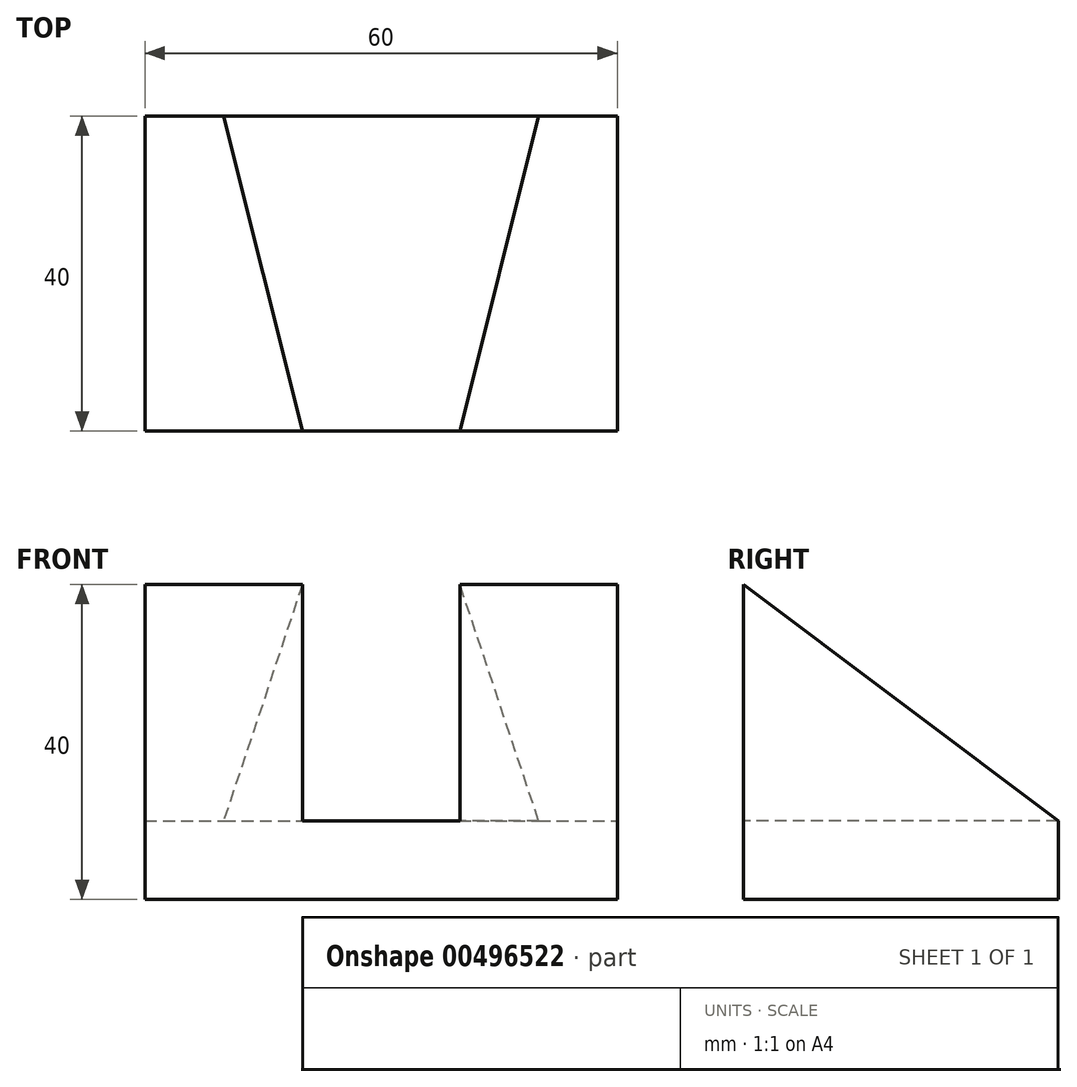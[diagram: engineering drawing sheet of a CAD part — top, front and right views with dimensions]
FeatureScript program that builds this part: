
annotation { "Feature Type Name" : "Feature", "Feature Type Description" : "" }
export const myFeature = defineFeature(function(context is Context, id is Id, definition is map)
    precondition{}
    {
        {
            var Q0;
            Q0=qCreatedBy(makeId("Top.planeOp"),FACE);
            var sketch = newSketch(context, id + "F0", { "sketchPlane" : qUnion([Q0])});
            skLineSegment(sketch, "E0", {"start": v(0, 0) * mm, "end": v(0, 40) * mm});
            skLineSegment(sketch, "E1", {"start": v(0, 40) * mm, "end": v(60, 40) * mm});
            skLineSegment(sketch, "E2", {"start": v(60, 40) * mm, "end": v(60, 0) * mm});
            skLineSegment(sketch, "E3", {"start": v(60, 0) * mm, "end": v(0, 0) * mm});
            skSolve(sketch);
        }
        {
            var Q0;
            Q0 = qSketchRegion(id + "F0", true);
            extrude(context, id + "F1", {"entities" : qUnion([Q0]), "depth" : 10 * mm, "offsetDistance" : 25 * mm});
        }
        {
            var Q0;
            Q0=makeQuery(id+"F1.opExtrude","SWEPT_FACE",FACE,{"disambiguationData":[OSD([sQuery(id+"F0.wireOp",EDGE,"E0")])]});
            var sketch = newSketch(context, id + "F2", { "sketchPlane" : qUnion([Q0])});
            skLineSegment(sketch, "E4", {"start": v(0, 10) * mm, "end": v(0, 40) * mm});
            skLineSegment(sketch, "E5", {"start": v(0, 40) * mm, "end": v(-40, 10) * mm});
            skLineSegment(sketch, "E6", {"start": v(-40, 10) * mm, "end": v(0, 10) * mm});
            skSolve(sketch);
        }
        {
            var Q0;
            Q0 = qSketchRegion(id + "F2", true);
            extrude(context, id + "F3", {"entities" : qUnion([Q0]), "operationType" : NewBodyOperationType.ADD, "depth" : -20 * mm, "offsetDistance" : 25 * mm});
        }
        {
            var Q0;
            Q0=makeQuery(id+"F1.opExtrude","SWEPT_FACE",FACE,{"disambiguationData":[OSD([sQuery(id+"F0.wireOp",EDGE,"E2")])]});
            var sketch = newSketch(context, id + "F4", { "sketchPlane" : qUnion([Q0])});
            skLineSegment(sketch, "E7", {"start": v(0, 10) * mm, "end": v(0, 40) * mm});
            skLineSegment(sketch, "E8", {"start": v(0, 40) * mm, "end": v(40, 10) * mm});
            skLineSegment(sketch, "E9", {"start": v(40, 10) * mm, "end": v(0, 10) * mm});
            skSolve(sketch);
        }
        {
            var Q0;
            Q0 = qSketchRegion(id + "F4", true);
            extrude(context, id + "F5", {"entities" : qUnion([Q0]), "operationType" : NewBodyOperationType.ADD, "depth" : -20 * mm, "offsetDistance" : 25 * mm});
        }
        {
            var Q0;
            Q0=makeQuery(id+"F1.opExtrude","CAP_FACE",FACE,{"disambiguationData":[OSD([sQuery(id+"F0.wireOp",EDGE,"E0"),sQuery(id+"F0.wireOp",EDGE,"E1"),sQuery(id+"F0.wireOp",EDGE,"E2"),sQuery(id+"F0.wireOp",EDGE,"E3")])],"isStart":false});
            var sketch = newSketch(context, id + "F6", { "sketchPlane" : qUnion([Q0])});
            skLineSegment(sketch, "E10", {"start": v(20, 0) * mm, "end": v(20, 40) * mm});
            skLineSegment(sketch, "E11", {"start": v(20, 40) * mm, "end": v(10, 40) * mm});
            skLineSegment(sketch, "E12", {"start": v(10, 40) * mm, "end": v(20, 0) * mm});
            skSolve(sketch);
        }
        {
            var Q0;
            Q0 = qSketchRegion(id + "F6", true);
            extrude(context, id + "F7", {"entities" : qUnion([Q0]), "operationType" : NewBodyOperationType.REMOVE, "oppositeDirection" : true, "depth" : -30 * mm, "offsetDistance" : 25 * mm});
        }
        {
            var Q0;
            Q0=makeQuery(id+"F7.boolean.opBoolean","MERGE",FACE,{"derivedFrom":[makeQuery(id+"F1.opExtrude","CAP_FACE",FACE,{"disambiguationData":[OSD([sQuery(id+"F0.wireOp",EDGE,"E0"),sQuery(id+"F0.wireOp",EDGE,"E1"),sQuery(id+"F0.wireOp",EDGE,"E2"),sQuery(id+"F0.wireOp",EDGE,"E3")])],"isStart":false}),makeQuery(id+"F7.opExtrude","CAP_FACE",FACE,{"disambiguationData":[OSD([sQuery(id+"F6.wireOp",EDGE,"E10"),sQuery(id+"F6.wireOp",EDGE,"E11"),sQuery(id+"F6.wireOp",EDGE,"E12")])],"isStart":true})]});
            var sketch = newSketch(context, id + "F8", { "sketchPlane" : qUnion([Q0])});
            skLineSegment(sketch, "E13", {"start": v(40, 0) * mm, "end": v(40, 40) * mm});
            skLineSegment(sketch, "E14", {"start": v(40, 40) * mm, "end": v(50, 40) * mm});
            skLineSegment(sketch, "E15", {"start": v(50, 40) * mm, "end": v(40, 0) * mm});
            skSolve(sketch);
        }
        {
            var Q0;
            Q0 = qSketchRegion(id + "F8", true);
            extrude(context, id + "F9", {"entities" : qUnion([Q0]), "operationType" : NewBodyOperationType.REMOVE, "oppositeDirection" : true, "depth" : -30 * mm, "offsetDistance" : 25 * mm});
        }
    });
